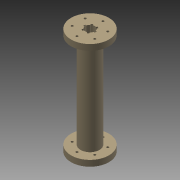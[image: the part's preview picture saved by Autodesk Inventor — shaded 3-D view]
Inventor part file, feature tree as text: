
AUTODESK INVENTOR PART (.ipt)
format: ipt  version: 2015 (Build 190159000, 159)  size: 138,240 bytes
history: native  units: mm
features: extrude x5, sketch x5, pattern_circular x2, pattern_linear x1
ambient origin geometry x8: Origin, YZ Plane, XZ Plane, XY Plane, X Axis, Y Axis, Z Axis, Center Point
bodies: 实体1 (feature_tree)
feature tree (13):
  extrude  "拉伸1"  Depth=25.0mm TaperAngle=0.0deg
  extrude  "拉伸2"  Depth=400.0mm TaperAngle=0.0deg
  extrude  "拉伸3"  Depth=55.0mm
  pattern_circular  "环形阵列1"  Count=40  [1 undecoded]
  pattern_linear  "矩形阵列1"  Count1=6 Spacing1=360.0deg
  extrude  "拉伸4"  Depth=40.0mm
  extrude  "拉伸5"  Depth=400.0mm
  pattern_circular  "环形阵列2"  [2 undecoded]
  sketch  "草图1"  dims[d0=160.0mm d1=25.0mm d2=0.0mm]
  sketch  "草图2"  dims[d3=80.0mm d4=400.0mm d5=0.0mm]
  sketch  "草图3"  dims[d6=9.146256mm d7=55.0mm d8=400.0mm d9=0.0mm d10=60.0mm d11=360.0deg]
  sketch  "草图4"  dims[d13=20.0mm d15=425.0mm d16=40.0mm]
  sketch  "草图5"  dims[d17=400.0mm d18=0.0mm d19=50.0mm d20=7.520077mm d21=4.0mm d22=8.0mm d23=400.0mm d24=0.0mm d25=60.0mm d26=360.0deg]
note: 3 required parameter values undecoded (feature->parameter linkage not recoverable at this tier; creation-order binding heuristic only, values carry confidence <= 0.55)
